# Revit family: ASTARIO
name_source: partatom
category: Luminaires
units: mm (PartAtom-declared; Revit-internal decimal feet)

## family parameters
Cote de connecteur circulaire = Utiliser le diamètre
Couper avec des vides une fois chargée = Oui
Hôte = Face
Numéro OmniClass = 23.80.70.11.14.21
Partagée = Oui
Point de calcul de pièce = Oui
Source d'éclairage = Oui
Titre OmniClass = Spots and Tracklight Specialties
Type d'élément = Normal

## types (2) — shared parameters
Angle de l'inclinaison = 60.00°
Charge apparente = 7 VA
Commentaires relatifs à la puissance = 6.3W
Description = Spot équipé d'une platine LED, efficacité lumineuse de 87.6lm/W
Diamètre intérieur = 33 mm  [stored 0.108268 ft]
Emettre la visibilité des formes dans le rendu = Non
Emettre à partir du diamètre du cercle = 610 mm
Fabricant = Résistex
Fichier de distribution photométrique = 963350.ies
Filtre de couleur = 16777215
Garantie = 5 ans
Gradation des changements de température de couleur de lampe = <Aucun>
IK = 07
IP = 65
Image du type = <Aucun>
Indice de charge = Eclairage
Matériau collerette = PC Transparent
Modèle = Astario
Nombre pôles = 1
Rayon collerette = 44 mm  [stored 0.144357 ft]
Rayon corps = 33 mm  [stored 0.108268 ft]
Tension = 230 V
URL = https://www.resistex-sa.com
Épaisseur = 33 mm  [stored 0.108268 ft]
Épaisseur collerette = 7 mm  [stored 0.0229659 ft]
zero-valued in all types: Elévation par défaut

## per-type parameters (varying)
| type | Coût |
| 963350 / 963351 | 32.5 $ |
| 963350 / 963352 | 40 $ |

note: [stored X ft] marks values corroborated as IEEE doubles in the binary element streams (Revit-internal decimal feet)
